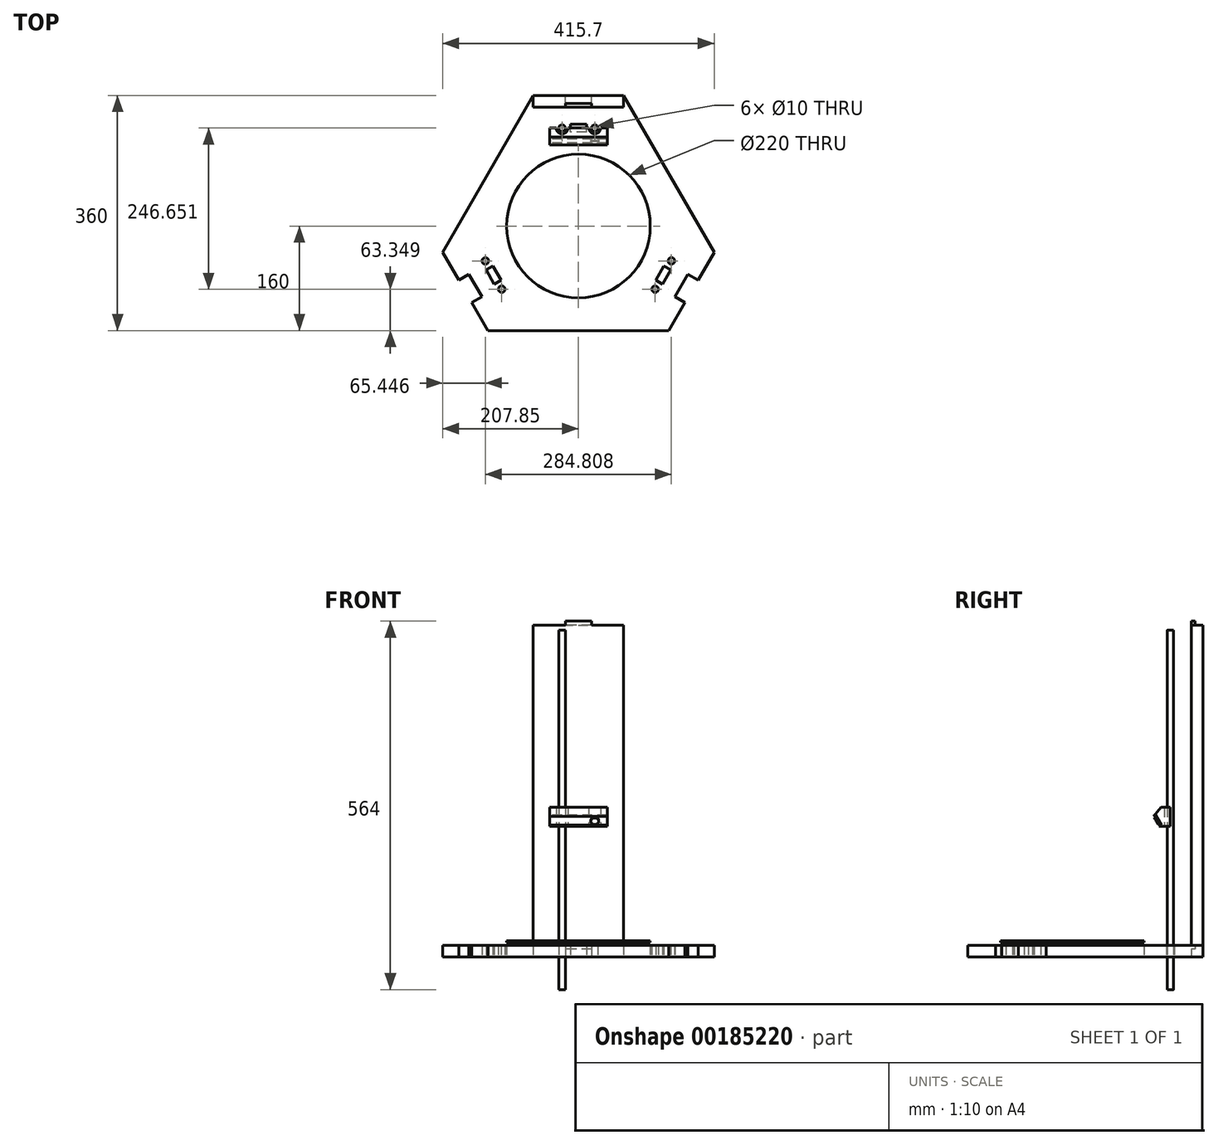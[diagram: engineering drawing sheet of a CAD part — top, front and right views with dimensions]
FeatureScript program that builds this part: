
annotation { "Feature Type Name" : "Feature", "Feature Type Description" : "" }
export const myFeature = defineFeature(function(context is Context, id is Id, definition is map)
    precondition{}
    {
        {
            var Q0;
            Q0=qCreatedBy(makeId("Top.planeOp"),FACE);
            var sketch = newSketch(context, id + "F0", { "sketchPlane" : qUnion([Q0])});
            skCircle(sketch, "E0", {"center": v(0, 0) * mm, "radius": 110 * mm});
            skCircle(sketch, "E1.cCircle", {"center": v(0, 0) * mm, "radius": 200 * mm, "construction": true});
            skLineSegment(sketch, "E1.0", {"start": v(-115.47, 200) * mm, "end": v(-69.28, 200) * mm, "construction": true});
            skLineSegment(sketch, "E1.1", {"start": v(115.47, 200) * mm, "end": v(230.94, 0) * mm, "construction": true});
            skLineSegment(sketch, "E1.2", {"start": v(230.94, 0) * mm, "end": v(207.85, -40) * mm, "construction": true});
            skLineSegment(sketch, "E1.3", {"start": v(115.47, -200) * mm, "end": v(-115.47, -200) * mm, "construction": true});
            skLineSegment(sketch, "E1.4", {"start": v(-115.47, -200) * mm, "end": v(-138.56, -160) * mm, "construction": true});
            skLineSegment(sketch, "E1.5", {"start": v(-230.94, 0) * mm, "end": v(-115.47, 200) * mm, "construction": true});
            skPoint(sketch, "E1.0.midPoint", {"position": v(0, 200) * mm});
            skCircle(sketch, "E2", {"center": v(-25, 150) * mm, "radius": 5 * mm});
            skCircle(sketch, "E3.MirrorC", {"center": v(25, 150) * mm, "radius": 5 * mm});
            skCircle(sketch, "E4.1.0", {"center": v(-117.4, -96.65) * mm, "radius": 5 * mm});
            skCircle(sketch, "E4.1.1", {"center": v(-142.4, -53.35) * mm, "radius": 5 * mm});
            skCircle(sketch, "E4.2.0", {"center": v(142.4, -53.35) * mm, "radius": 5 * mm});
            skCircle(sketch, "E4.2.1", {"center": v(117.4, -96.65) * mm, "radius": 5 * mm});
            skLineSegment(sketch, "E5", {"start": v(-69.28, 200) * mm, "end": v(-207.85, -40) * mm});
            skLineSegment(sketch, "E6", {"start": v(-138.56, -160) * mm, "end": v(138.56, -160) * mm});
            skLineSegment(sketch, "E7", {"start": v(69.28, 200) * mm, "end": v(69.28, 200) * mm});
            skLineSegment(sketch, "E8", {"start": v(-69.28, 200) * mm, "end": v(-20, 200) * mm});
            skLineSegment(sketch, "E9", {"start": v(-207.85, -40) * mm, "end": v(-230.94, 0) * mm, "construction": true});
            skLineSegment(sketch, "E10", {"start": v(138.56, -160) * mm, "end": v(115.47, -200) * mm, "construction": true});
            skLineSegment(sketch, "E11", {"start": v(-138.56, -160) * mm, "end": v(-163.2, -117.32) * mm});
            skLineSegment(sketch, "E12", {"start": v(207.85, -40) * mm, "end": v(183.2, -82.68) * mm});
            skLineSegment(sketch, "E13", {"start": v(69.28, 200) * mm, "end": v(207.85, -40) * mm});
            skLineSegment(sketch, "E14", {"start": v(69.28, 200) * mm, "end": v(115.47, 200) * mm, "construction": true});
            skLineSegment(sketch, "E15.bottom", {"start": v(20, 182) * mm, "end": v(-20, 182) * mm});
            skLineSegment(sketch, "E15.left", {"start": v(20, 182) * mm, "end": v(20, 200) * mm});
            skLineSegment(sketch, "E15.right", {"start": v(-20, 182) * mm, "end": v(-20, 200) * mm});
            skPoint(sketch, "E16.orphan", {"position": v(20, 218) * mm});
            skPoint(sketch, "E17.orphan", {"position": v(-20, 218) * mm});
            skLineSegment(sketch, "E18.trimOffspring", {"start": v(20, 200) * mm, "end": v(69.28, 200) * mm});
            skLineSegment(sketch, "E19.1.0", {"start": v(-147.62, -108.32) * mm, "end": v(-163.2, -117.32) * mm});
            skLineSegment(sketch, "E19.1.1", {"start": v(-167.62, -73.68) * mm, "end": v(-147.62, -108.32) * mm});
            skLineSegment(sketch, "E19.1.2", {"start": v(-167.62, -73.68) * mm, "end": v(-183.2, -82.68) * mm});
            skLineSegment(sketch, "E19.2.0", {"start": v(167.62, -73.68) * mm, "end": v(183.2, -82.68) * mm});
            skLineSegment(sketch, "E19.2.1", {"start": v(147.62, -108.32) * mm, "end": v(167.62, -73.68) * mm});
            skLineSegment(sketch, "E19.2.2", {"start": v(147.62, -108.32) * mm, "end": v(163.2, -117.32) * mm});
            skLineSegment(sketch, "E20.trimOffspring", {"start": v(163.2, -117.32) * mm, "end": v(138.56, -160) * mm});
            skLineSegment(sketch, "E21.trimOffspring", {"start": v(-183.2, -82.68) * mm, "end": v(-207.85, -40) * mm});
            skLineSegment(sketch, "E22", {"start": v(-25, 150) * mm, "end": v(25, 150) * mm, "construction": true});
            skLineSegment(sketch, "E23.bottom", {"start": v(12.5, 144) * mm, "end": v(-12.5, 144) * mm});
            skLineSegment(sketch, "E23.top", {"start": v(12.5, 156) * mm, "end": v(-12.5, 156) * mm});
            skLineSegment(sketch, "E23.left", {"start": v(12.5, 144) * mm, "end": v(12.5, 156) * mm});
            skLineSegment(sketch, "E23.right", {"start": v(-12.5, 144) * mm, "end": v(-12.5, 156) * mm});
            skPoint(sketch, "E23.middle", {"position": v(0, 150) * mm});
            skLineSegment(sketch, "E24.1.0", {"start": v(-130.96, -61.17) * mm, "end": v(-118.46, -82.83) * mm});
            skLineSegment(sketch, "E24.1.1", {"start": v(-130.96, -61.17) * mm, "end": v(-141.35, -67.17) * mm});
            skLineSegment(sketch, "E24.1.2", {"start": v(-141.35, -67.17) * mm, "end": v(-128.85, -88.83) * mm});
            skLineSegment(sketch, "E24.1.3", {"start": v(-118.46, -82.83) * mm, "end": v(-128.85, -88.83) * mm});
            skLineSegment(sketch, "E24.2.0", {"start": v(118.46, -82.83) * mm, "end": v(130.96, -61.17) * mm});
            skLineSegment(sketch, "E24.2.1", {"start": v(118.46, -82.83) * mm, "end": v(128.85, -88.83) * mm});
            skLineSegment(sketch, "E24.2.2", {"start": v(128.85, -88.83) * mm, "end": v(141.35, -67.17) * mm});
            skLineSegment(sketch, "E24.2.3", {"start": v(130.96, -61.17) * mm, "end": v(141.35, -67.17) * mm});
            skSolve(sketch);
        }
        {
            var Q0;
            Q0=makeQuery(id+"F0.imprint","IMPRINT",FACE,{"disambiguationData":[TD([[makeQuery(id+"F0.imprint","IMPRINT",EDGE,{"derivedFrom":sQuery(id+"F0.wireOp",EDGE,"E0")}),-1.0]])]});
            extrude(context, id + "F1", {"entities" : qUnion([Q0]), "depth" : 18 * mm, "offsetDistance" : 25 * mm});
        }
        {
            var Q0;
            Q0=makeQuery(id+"F0.imprint","IMPRINT",FACE,{"disambiguationData":[TD([[makeQuery(id+"F0.imprint","IMPRINT",EDGE,{"derivedFrom":sQuery(id+"F0.wireOp",EDGE,"E2")}),1.0]])]});
            extrude(context, id + "F2", {"entities" : qUnion([Q0]), "depth" : 500 * mm, "hasSecondDirection" : true, "secondDirectionOppositeDirection" : true, "secondDirectionDepth" : 50 * mm});
        }
        {
            var Q0;
            Q0=makeQuery(id+"F0.imprint","IMPRINT",FACE,{"disambiguationData":[TD([[makeQuery(id+"F0.imprint","IMPRINT",EDGE,{"derivedFrom":sQuery(id+"F0.wireOp",EDGE,"E0")}),1.0]])]});
            extrude(context, id + "F3", {"entities" : qUnion([Q0]), "depth" : 25 * mm, "hasSecondDirection" : true, "secondDirectionOppositeDirection" : false, "secondDirectionDepth" : (25 - 3) * mm});
        }
        {
            var Q0;
            Q0=makeQuery(id+"F1.opExtrude","CAP_FACE",FACE,{"disambiguationData":[OSD([sQuery(id+"F0.wireOp",EDGE,"E1.0"),sQuery(id+"F0.wireOp",EDGE,"E1.1"),sQuery(id+"F0.wireOp",EDGE,"E1.2"),sQuery(id+"F0.wireOp",EDGE,"E1.3"),sQuery(id+"F0.wireOp",EDGE,"E1.4"),sQuery(id+"F0.wireOp",EDGE,"E1.5"),sQuery(id+"F0.wireOp",EDGE,"E2"),sQuery(id+"F0.wireOp",EDGE,"E3.MirrorC"),sQuery(id+"F0.wireOp",EDGE,"E4.1.0"),sQuery(id+"F0.wireOp",EDGE,"E4.1.1"),sQuery(id+"F0.wireOp",EDGE,"E4.2.0"),sQuery(id+"F0.wireOp",EDGE,"E4.2.1")])],"isStart":false});
            var sketch = newSketch(context, id + "F4", { "sketchPlane" : qUnion([Q0])});
            skLineSegment(sketch, "E25.0", {"start": v(-69.28, 200) * mm, "end": v(69.28, 200) * mm});
            skLineSegment(sketch, "E26", {"start": v(69.28, 200) * mm, "end": v(69.28, 182) * mm});
            skLineSegment(sketch, "E27", {"start": v(69.28, 182) * mm, "end": v(-69.28, 182) * mm});
            skLineSegment(sketch, "E28", {"start": v(-69.28, 182) * mm, "end": v(-69.28, 200) * mm});
            skSolve(sketch);
        }
        {
            var Q0;
            Q0=makeQuery(id+"F4.imprint","IMPRINT",FACE,{"disambiguationData":[TD([[makeQuery(id+"F4.imprint","IMPRINT",EDGE,{"derivedFrom":sQuery(id+"F4.wireOp",EDGE,"E25.0")}),-1.0]])]});
            extrude(context, id + "F5", {"entities" : qUnion([Q0]), "depth" : 490 * mm, "offsetDistance" : 25 * mm});
        }
        {
            var Q0;
            Q0=makeQuery(id+"F5.opExtrude","SWEPT_FACE",FACE,{"disambiguationData":[OSD([sQuery(id+"F4.wireOp",EDGE,"E27")])]});
            var sketch = newSketch(context, id + "F6", { "sketchPlane" : qUnion([Q0])});
            skLineSegment(sketch, "E29.0", {"start": v(69.28, 18) * mm, "end": v(-69.28, 18) * mm, "construction": true});
            skLineSegment(sketch, "E30.bottom", {"start": v(20, 18) * mm, "end": v(-20, 18) * mm});
            skLineSegment(sketch, "E30.top", {"start": v(20, 12) * mm, "end": v(-20, 12) * mm});
            skLineSegment(sketch, "E30.left", {"start": v(20, 18) * mm, "end": v(20, 12) * mm});
            skLineSegment(sketch, "E30.right", {"start": v(-20, 18) * mm, "end": v(-20, 12) * mm});
            skPoint(sketch, "E30.middle", {"position": v(0, 15) * mm});
            skPoint(sketch, "E30.middle.positionSnap0", {"position": v(0, 18) * mm});
            skPoint(sketch, "E30.centerSnap0", {"position": v(0, 18) * mm});
            skLineSegment(sketch, "E31.0", {"start": v(69.28, 508) * mm, "end": v(69.28, 18) * mm, "construction": true});
            skLineSegment(sketch, "E31.1", {"start": v(-69.28, 508) * mm, "end": v(-69.28, 18) * mm, "construction": true});
            skLineSegment(sketch, "E32", {"start": v(-69.28, 263) * mm, "end": v(69.28, 263) * mm, "construction": true});
            skLineSegment(sketch, "E33.MirrorCS", {"start": v(20, 508) * mm, "end": v(20, 514) * mm});
            skLineSegment(sketch, "E34.MirrorCS", {"start": v(20, 514) * mm, "end": v(-20, 514) * mm});
            skLineSegment(sketch, "E35.MirrorCS", {"start": v(-20, 508) * mm, "end": v(-20, 514) * mm});
            skLineSegment(sketch, "E36", {"start": v(-20, 508) * mm, "end": v(20, 508) * mm});
            skSolve(sketch);
        }
        {
            var Q0;
            Q0=makeQuery(id+"F6.imprint","IMPRINT",FACE,{"disambiguationData":[TD([[makeQuery(id+"F6.imprint","IMPRINT",EDGE,{"derivedFrom":sQuery(id+"F6.wireOp",EDGE,"E30.bottom")}),1.0]])]});
            var Q1;
            Q1=makeQuery(id+"F6.imprint","IMPRINT",FACE,{"disambiguationData":[TD([[makeQuery(id+"F6.imprint","IMPRINT",EDGE,{"derivedFrom":sQuery(id+"F6.wireOp",EDGE,"E33.MirrorCS")}),1.0]])]});
            extrude(context, id + "F7", {"entities" : qUnion([Q0, Q1]), "operationType" : NewBodyOperationType.ADD, "oppositeDirection" : true, "depth" : 6 * mm});
        }
        {
            var Q0;
            Q0=qCreatedBy(makeId("Top.planeOp"),FACE);
            cPlane(context, id + "F8", {"entities" : qUnion([Q0]), "cplaneType" : CPlaneType.OFFSET, "offset" : 200 * mm, "width" : 150 * mm, "height" : 150 * mm});
        }
        {
            var Q0;
            Q0=qCreatedBy(id+"F8.planeOp",FACE);
            var sketch = newSketch(context, id + "F9", { "sketchPlane" : qUnion([Q0])});
            skArc(sketch, "E37.0", {"start": v(-34, 150) * mm, "mid": v(-25, 141) * mm, "end": v(-16, 150) * mm});
            skLineSegment(sketch, "E38.0", {"start": v(-25, 150) * mm, "end": v(25, 150) * mm, "construction": true});
            skLineSegment(sketch, "E39", {"start": v(0, 150) * mm, "end": v(0, 162.54) * mm, "construction": true});
            skLineSegment(sketch, "E40", {"start": v(-34, 150) * mm, "end": v(-44, 150) * mm});
            skLineSegment(sketch, "E41", {"start": v(-44, 150) * mm, "end": v(-44, 136) * mm});
            skLineSegment(sketch, "E42.MirrorCS", {"start": v(34, 150) * mm, "end": v(44, 150) * mm});
            skLineSegment(sketch, "E43.MirrorCS", {"start": v(44, 150) * mm, "end": v(44, 136) * mm});
            skArc(sketch, "E44.MirrorC", {"start": v(34, 150) * mm, "mid": v(25, 141) * mm, "end": v(16, 150) * mm});
            skLineSegment(sketch, "E45", {"start": v(-44, 136) * mm, "end": v(44, 136) * mm});
            skLineSegment(sketch, "E46", {"start": v(-16, 150) * mm, "end": v(16, 150) * mm});
            skLineSegment(sketch, "E47", {"start": v(-25, 150) * mm, "end": v(-25, 127.7) * mm, "construction": true});
            skPoint(sketch, "E47.endSnap0", {"position": v(-25, 141) * mm});
            skCircle(sketch, "E48", {"center": v(-25, 136) * mm, "radius": 6 * mm, "construction": true});
            skSolve(sketch);
        }
        {
            var Q0;
            Q0=makeQuery(id+"F9.imprint","IMPRINT",FACE,{"disambiguationData":[TD([[makeQuery(id+"F9.imprint","IMPRINT",EDGE,{"derivedFrom":sQuery(id+"F9.wireOp",EDGE,"E37.0")}),-1.0]])]});
            extrude(context, id + "F10", {"entities" : qUnion([Q0]), "depth" : 29 * mm});
        }
        {
            var Q0;
            Q0=makeQuery(id+"F10.opExtrude","SWEPT_FACE",FACE,{"disambiguationData":[OSD([sQuery(id+"F9.wireOp",EDGE,"E41")])]});
            var sketch = newSketch(context, id + "F11", { "sketchPlane" : qUnion([Q0])});
            skLineSegment(sketch, "E49", {"start": v(-135.06, 204.31) * mm, "end": v(-129.06, 214.7) * mm});
            skLineSegment(sketch, "E50", {"start": v(-129.06, 214.7) * mm, "end": v(-125.6, 212.7) * mm});
            skLineSegment(sketch, "E51", {"start": v(-125.6, 212.7) * mm, "end": v(-131.6, 202.31) * mm});
            skLineSegment(sketch, "E52", {"start": v(-131.6, 202.31) * mm, "end": v(-135.06, 204.31) * mm});
            skLineSegment(sketch, "E53.0", {"start": v(-136, 229) * mm, "end": v(-136, 200) * mm});
            skLineSegment(sketch, "E54", {"start": v(-125.6, 212.7) * mm, "end": v(-124.26, 215.01) * mm});
            skLineSegment(sketch, "E55", {"start": v(-124.26, 215.01) * mm, "end": v(-136, 229) * mm});
            skLineSegment(sketch, "E56", {"start": v(-131.6, 202.31) * mm, "end": v(-132.93, 200) * mm});
            skLineSegment(sketch, "E57", {"start": v(-132.93, 200) * mm, "end": v(-136, 200) * mm});
            skLineSegment(sketch, "E58", {"start": v(-132.06, 209.5) * mm, "end": v(-126, 206) * mm, "construction": true});
            skSolve(sketch);
        }
        {
            var Q0;
            {var subQ2=sQuery(id+"F11.wireOp",EDGE,"E49");Q0=makeQuery(id+"F11.imprint","IMPRINT",FACE,{"disambiguationData":[TD([[makeQuery(id+"F11.imprint","IMPRINT",EDGE,{"derivedFrom":subQ2}),1.0]])]});}
            var Q1;
            Q1=makeQuery(id+"F11.imprint","IMPRINT",FACE,{"disambiguationData":[TD([[makeQuery(id+"F11.imprint","IMPRINT",EDGE,{"derivedFrom":sQuery(id+"F11.wireOp",EDGE,"E49")}),-1.0]])]});
            var Q2;
            {var subQ0=sQuery(id+"F11.wireOp",EDGE,"E52");Q2=makeQuery(id+"F11.imprint","IMPRINT",FACE,{"disambiguationData":[TD([[makeQuery(id+"F11.imprint","IMPRINT",EDGE,{"derivedFrom":subQ0}),1.0]])]});}
            extrude(context, id + "F12", {"entities" : qUnion([Q0, Q1, Q2]), "operationType" : NewBodyOperationType.ADD, "oppositeDirection" : true, "depth" : 88 * mm});
        }
        {
            var Q0;
            Q0=makeQuery(id+"F12.opExtrude","SWEPT_FACE",FACE,{"disambiguationData":[OSD([sQuery(id+"F11.wireOp",EDGE,"E51"),sQuery(id+"F11.wireOp",EDGE,"E54"),sQuery(id+"F11.wireOp",EDGE,"E56")])]});
            var sketch = newSketch(context, id + "F13", { "sketchPlane" : qUnion([Q0])});
            skLineSegment(sketch, "E59.0", {"start": v(44, 124.08) * mm, "end": v(-44, 124.08) * mm, "construction": true});
            skLineSegment(sketch, "E59.1", {"start": v(44, 106.74) * mm, "end": v(-44, 106.74) * mm, "construction": true});
            skLineSegment(sketch, "E60.0", {"start": v(-25, -75) * mm, "end": v(25, -75) * mm, "construction": true});
            skLineSegment(sketch, "E61", {"start": v(0, 124.08) * mm, "end": v(0, 106.74) * mm, "construction": true});
            skLineSegment(sketch, "E62", {"start": v(0, 115.4) * mm, "end": v(-25, 115.4) * mm, "construction": true});
            skCircle(sketch, "E63", {"center": v(-25, 115.4) * mm, "radius": 6 * mm});
            skCircle(sketch, "E64.MirrorC", {"center": v(25, 115.4) * mm, "radius": 6 * mm});
            skSolve(sketch);
        }
        {
            var Q0;
            Q0=makeQuery(id+"F13.imprint","IMPRINT",FACE,{"disambiguationData":[TD([[makeQuery(id+"F13.imprint","IMPRINT",EDGE,{"derivedFrom":sQuery(id+"F13.wireOp",EDGE,"E63")}),1.0]])]});
            var Q1;
            Q1=makeQuery(id+"F13.imprint","IMPRINT",FACE,{"disambiguationData":[TD([[makeQuery(id+"F13.imprint","IMPRINT",EDGE,{"derivedFrom":sQuery(id+"F13.wireOp",EDGE,"E64.MirrorC")}),-1.0]])]});
            extrude(context, id + "F14", {"entities" : qUnion([Q0, Q1]), "operationType" : NewBodyOperationType.REMOVE, "oppositeDirection" : true, "depth" : 4 * mm});
        }
    });
